# Revit family: VLGFP1002-xxxWS8xxA09xx
name_source: partatom
category: Oprawy oświetleniowe
revit_build: Autodesk Revit 2017 (Build: 20190508_0315(x64)
units: mm (PartAtom-declared; Revit-internal decimal feet)

## family parameters
Numer OmniClass = 23.80.70.11
Obiekt nadrzędny = Powierzchnia
Punkt obliczania pomieszczeń = Nie
Tnij formami wycięć po wczytaniu = Nie
Typ części = Normalny
Tytuł OmniClass = Luminaries for Internal Lighting
Współdzielony = Nie
Wymiar okrągłego złącza = Użyj średnicy
Źródło światła = Tak

## types (8) — shared parameters
Emituj kształt widoczny w renderingu = Nie
Filtr koloru = 16777215
Kod zespołu = D5020200
Lampa = LED
Obciążenie pozorne = 66 VA
Odchylenie kierunku = 90.00°
Plik sieci fotometrycznej = VLGFP1502-5NDWS840A1400.IES
Producent = RIDI Leuchten GmbH
URL = www.ridi.de
Zmiana temperatury barwowej przyciemniania lampy = <Brak>
brand = RIDI
conformity mark = CE
electrical safety class = 1
height = 66 mm  [stored 0.216535 ft]
ingress protection (IP) code = IP54
length = 1000 mm  [stored 3.28084 ft]
nominal frequency = 50-60Hz
nominal voltage = 230
rated input power = 66
voltage type (AC, DC, UC) = AC
weight = 1.64 kg
width = 67 mm
zero-valued in all types: Domyślna rzędna

## per-type parameters (varying)
| type | Emituj z długości prostokąta | Emituj z szerokości prostokąta | Model |
| VLGFP1002-5NDWS830A0900 | 63 mm  [stored 0.206693 ft] | 969 mm | 1551034 |
| VLGFP1002-7DAWS830A0900 | 63 mm  [stored 0.206693 ft] | 969 mm | 1561034 |
| VLGFP1002-7DAWS840A0950 | 63 mm  [stored 0.206693 ft] | 969 mm | 1561015 |
| VLGFP1002-5NDWS850A0950 | 63 mm  [stored 0.206693 ft] | 969 mm | 1551048 |
| VLGFP1002-7DAWS850A0950 | 63 mm  [stored 0.206693 ft] | 969 mm | 1561048 |
| VLGFP1002-5NDWS865A0950 | 63 mm  [stored 0.206693 ft] | 969 mm | 1551061 |
| VLGFP1002-7DAWS865A0950 | 57 mm  [stored 0.187008 ft] | 970 mm  [stored 3.18241 ft] | 1561061
1561061
1561061 |
| VLGFP1002-5NDWS840A0950 | 57 mm  [stored 0.187008 ft] | 970 mm  [stored 3.18241 ft] | 1551015 |

note: column(s) folded — value = type name in every type: product name

note: [stored X ft] marks values corroborated as IEEE doubles in the binary element streams (Revit-internal decimal feet)
